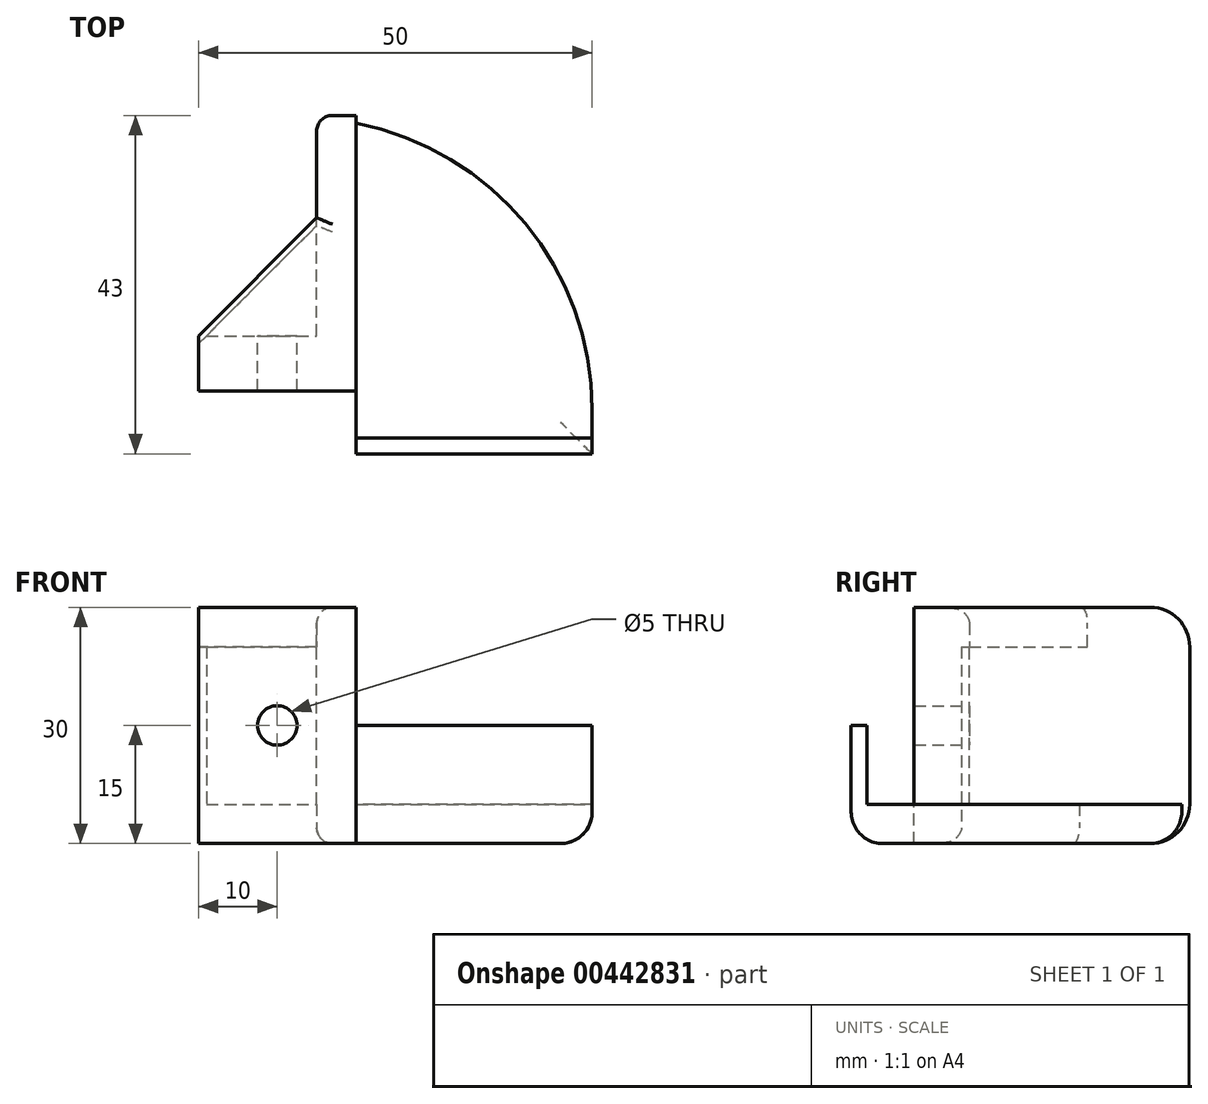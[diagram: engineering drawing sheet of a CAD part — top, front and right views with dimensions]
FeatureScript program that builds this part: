
annotation { "Feature Type Name" : "Feature", "Feature Type Description" : "" }
export const myFeature = defineFeature(function(context is Context, id is Id, definition is map)
    precondition{}
    {
        {
            var Q0;
            Q0=qCreatedBy(makeId("Top.planeOp"),FACE);
            var sketch = newSketch(context, id + "F0", { "sketchPlane" : qUnion([Q0])});
            skLineSegment(sketch, "E0.bottom", {"start": v(0, 0) * mm, "end": v(30, 0) * mm});
            skLineSegment(sketch, "E0.top", {"start": v(0, 42) * mm, "end": v(30, 42) * mm});
            skLineSegment(sketch, "E0.left", {"start": v(0, 0) * mm, "end": v(0, 42) * mm});
            skLineSegment(sketch, "E0.right", {"start": v(30, 0) * mm, "end": v(30, 42) * mm});
            skSolve(sketch);
        }
        {
            var Q0;
            Q0=makeQuery(id+"F0.imprint","IMPRINT",FACE,{"disambiguationData":[TD([[makeQuery(id+"F0.imprint","IMPRINT",EDGE,{"derivedFrom":sQuery(id+"F0.wireOp",EDGE,"E0.bottom")}),1.0]])]});
            extrude(context, id + "F1", {"entities" : qUnion([Q0]), "depth" : 5 * mm});
        }
        {
            var Q0;
            Q0=makeQuery(id+"F1.opExtrude","SWEPT_EDGE",EDGE,{"disambiguationData":[OSD([sQuery(id+"F0.wireOp",EDGE,"E0.top"),sQuery(id+"F0.wireOp",EDGE,"E0.right")])]});
            fillet(context, id + "F2", {"entities" : qUnion([Q0]), "radius" : 37 * mm, "tangentPropagation" : true, "allowEdgeOverflow" : false});
        }
        {
            var Q0;
            Q0=makeQuery(id+"F1.opExtrude","CAP_FACE",FACE,{"disambiguationData":[OSD([sQuery(id+"F0.wireOp",EDGE,"E0.bottom"),sQuery(id+"F0.wireOp",EDGE,"E0.top"),sQuery(id+"F0.wireOp",EDGE,"E0.left"),sQuery(id+"F0.wireOp",EDGE,"E0.right")])],"isStart":false});
            var sketch = newSketch(context, id + "F3", { "sketchPlane" : qUnion([Q0])});
            skLineSegment(sketch, "E1.bottom", {"start": v(0, 0) * mm, "end": v(30, 0) * mm});
            skLineSegment(sketch, "E1.top", {"start": v(0, 2) * mm, "end": v(30, 2) * mm});
            skLineSegment(sketch, "E1.left", {"start": v(0, 0) * mm, "end": v(0, 2) * mm});
            skLineSegment(sketch, "E1.right", {"start": v(30, 0) * mm, "end": v(30, 2) * mm});
            skSolve(sketch);
        }
        {
            var Q0;
            Q0=qSketchRegion(id+"F3",true);
            extrude(context, id + "F4", {"entities" : qUnion([Q0]), "operationType" : NewBodyOperationType.ADD, "depth" : 10 * mm});
        }
        {
            var Q0;
            Q0=makeQuery(id+"F4.boolean.opBoolean","MERGE",FACE,{"derivedFrom":[makeQuery(id+"F1.opExtrude","SWEPT_FACE",FACE,{"disambiguationData":[OSD([sQuery(id+"F0.wireOp",EDGE,"E0.left")])]}),makeQuery(id+"F4.opExtrude","SWEPT_FACE",FACE,{"disambiguationData":[OSD([sQuery(id+"F3.wireOp",EDGE,"E1.left")])]})]});
            var sketch = newSketch(context, id + "F5", { "sketchPlane" : qUnion([Q0])});
            skLineSegment(sketch, "E2.bottom", {"start": v(-8, 0) * mm, "end": v(-43, 0) * mm});
            skLineSegment(sketch, "E2.top", {"start": v(-8, 30) * mm, "end": v(-43, 30) * mm});
            skLineSegment(sketch, "E2.left", {"start": v(-8, 0) * mm, "end": v(-8, 30) * mm});
            skLineSegment(sketch, "E2.right", {"start": v(-43, 0) * mm, "end": v(-43, 30) * mm});
            skSolve(sketch);
        }
        {
            var Q0;
            Q0=qSketchRegion(id+"F5",true);
            extrude(context, id + "F6", {"entities" : qUnion([Q0]), "operationType" : NewBodyOperationType.ADD, "depth" : 5 * mm});
        }
        {
            var Q0;
            Q0=makeQuery(id+"F6.opExtrude","CAP_FACE",FACE,{"disambiguationData":[OSD([sQuery(id+"F5.wireOp",EDGE,"E2.bottom"),sQuery(id+"F5.wireOp",EDGE,"E2.top"),sQuery(id+"F5.wireOp",EDGE,"E2.left"),sQuery(id+"F5.wireOp",EDGE,"E2.right")])],"isStart":false});
            var sketch = newSketch(context, id + "F7", { "sketchPlane" : qUnion([Q0])});
            skLineSegment(sketch, "E3.bottom", {"start": v(-8, 0) * mm, "end": v(-8, 0) * mm});
            skLineSegment(sketch, "E3.top", {"start": v(-8, 30) * mm, "end": v(-8, 30) * mm});
            skLineSegment(sketch, "E3.left", {"start": v(-8, 0) * mm, "end": v(-8, 30) * mm});
            skLineSegment(sketch, "E3.right", {"start": v(-8, 0) * mm, "end": v(-8, 30) * mm});
            skLineSegment(sketch, "E4.bottom", {"start": v(-8, 0) * mm, "end": v(-15, 0) * mm});
            skLineSegment(sketch, "E4.top", {"start": v(-8, 30) * mm, "end": v(-15, 30) * mm});
            skLineSegment(sketch, "E4.right", {"start": v(-15, 0) * mm, "end": v(-15, 30) * mm});
            skSolve(sketch);
        }
        {
            var Q0;
            Q0=qSketchRegion(id+"F7",true);
            extrude(context, id + "F8", {"entities" : qUnion([Q0]), "operationType" : NewBodyOperationType.ADD, "depth" : 15 * mm});
        }
        {
            var Q0;
            Q0=makeQuery(id+"F8.opExtrude","SWEPT_FACE",FACE,{"disambiguationData":[OSD([sQuery(id+"F7.wireOp",EDGE,"E4.right")])]});
            var sketch = newSketch(context, id + "F9", { "sketchPlane" : qUnion([Q0])});
            skCircle(sketch, "E5", {"center": v(10, 15) * mm, "radius": 2.5 * mm});
            skSolve(sketch);
        }
        {
            var Q0;
            Q0=makeQuery(id+"F9.imprint","IMPRINT",FACE,{"disambiguationData":[TD([[makeQuery(id+"F9.imprint","IMPRINT",EDGE,{"derivedFrom":sQuery(id+"F9.wireOp",EDGE,"E5")}),1.0]])]});
            var Q1;
            Q1=sQuery(id+"F9.wireOp",EDGE,"E5");
            extrude(context, id + "F10", {"entities" : qUnion([Q0]), "operationType" : NewBodyOperationType.REMOVE, "surfaceEntities" : qUnion([Q1]), "oppositeDirection" : true, "depth" : 10 * mm});
        }
        {
            var Q0;
            {var subQ0=sQuery(id+"F0.wireOp",EDGE,"E0.right");var subQ1=sQuery(id+"F0.wireOp",EDGE,"E0.top");Q0=makeQuery(id+"F2.opFillet","BLEND_EDGE",EDGE,{"blendedFrom":[makeQuery(id+"F1.opExtrude","SWEPT_EDGE",EDGE,{"disambiguationData":[OSD([subQ1,subQ0])]}),makeQuery(id+"F1.opExtrude","CAP_FACE",FACE,{"disambiguationData":[OSD([sQuery(id+"F0.wireOp",EDGE,"E0.bottom"),subQ1,sQuery(id+"F0.wireOp",EDGE,"E0.left"),subQ0])],"isStart":true})],"blendedInto":[makeQuery(id+"F1.opExtrude","CAP_FACE",FACE,{"disambiguationData":[OSD([sQuery(id+"F0.wireOp",EDGE,"E0.bottom"),subQ1,sQuery(id+"F0.wireOp",EDGE,"E0.left"),subQ0])],"isStart":true})]});}
            var Q1;
            Q1=makeQuery(id+"F1.opExtrude","CAP_EDGE",EDGE,{"disambiguationData":[OSD([sQuery(id+"F0.wireOp",EDGE,"E0.bottom")])],"isStart":true});
            fillet(context, id + "F11", {"entities" : qUnion([Q0, Q1]), "radius" : 4 * mm, "tangentPropagation" : true, "allowEdgeOverflow" : false});
        }
        {
            var Q0;
            Q0=makeQuery(id+"F8.boolean.opBoolean","MERGE",FACE,{"derivedFrom":[makeQuery(id+"F6.boolean.opBoolean","MERGE",FACE,{"derivedFrom":[makeQuery(id+"F1.opExtrude","CAP_FACE",FACE,{"disambiguationData":[OSD([sQuery(id+"F0.wireOp",EDGE,"E0.bottom"),sQuery(id+"F0.wireOp",EDGE,"E0.top"),sQuery(id+"F0.wireOp",EDGE,"E0.left"),sQuery(id+"F0.wireOp",EDGE,"E0.right")])],"isStart":true}),makeQuery(id+"F6.opExtrude","SWEPT_FACE",FACE,{"disambiguationData":[OSD([sQuery(id+"F5.wireOp",EDGE,"E2.bottom")])]})]}),makeQuery(id+"F8.opExtrude","SWEPT_FACE",FACE,{"disambiguationData":[OSD([sQuery(id+"F7.wireOp",EDGE,"E4.bottom")])]})]});
            var sketch = newSketch(context, id + "F12", { "sketchPlane" : qUnion([Q0])});
            skLineSegment(sketch, "E6.bottom", {"start": v(-20, -15) * mm, "end": v(-5, -15) * mm});
            skLineSegment(sketch, "E6.top", {"start": v(-20, -29) * mm, "end": v(-5, -29) * mm});
            skLineSegment(sketch, "E6.left", {"start": v(-20, -15) * mm, "end": v(-20, -29) * mm});
            skLineSegment(sketch, "E6.right", {"start": v(-5, -15) * mm, "end": v(-5, -29) * mm});
            skSolve(sketch);
        }
        {
            var Q0;
            Q0=makeQuery(id+"F12.imprint","IMPRINT",FACE,{"disambiguationData":[TD([[makeQuery(id+"F12.imprint","IMPRINT",EDGE,{"derivedFrom":sQuery(id+"F12.wireOp",EDGE,"E6.bottom")}),-1.0]])]});
            extrude(context, id + "F13", {"entities" : qUnion([Q0]), "operationType" : NewBodyOperationType.ADD, "oppositeDirection" : true, "depth" : 5 * mm});
        }
        {
            var Q0;
            Q0=makeQuery(id+"F8.boolean.opBoolean","MERGE",FACE,{"derivedFrom":[makeQuery(id+"F6.opExtrude","SWEPT_FACE",FACE,{"disambiguationData":[OSD([sQuery(id+"F5.wireOp",EDGE,"E2.top")])]}),makeQuery(id+"F8.opExtrude","SWEPT_FACE",FACE,{"disambiguationData":[OSD([sQuery(id+"F7.wireOp",EDGE,"E4.top")])]})]});
            var sketch = newSketch(context, id + "F14", { "sketchPlane" : qUnion([Q0])});
            skLineSegment(sketch, "E7.bottom", {"start": v(-5, 15) * mm, "end": v(-20, 15) * mm});
            skLineSegment(sketch, "E7.top", {"start": v(-5, 30) * mm, "end": v(-20, 30) * mm});
            skLineSegment(sketch, "E7.left", {"start": v(-5, 15) * mm, "end": v(-5, 30) * mm});
            skLineSegment(sketch, "E7.right", {"start": v(-20, 15) * mm, "end": v(-20, 30) * mm});
            skSolve(sketch);
        }
        {
            var Q0;
            Q0=makeQuery(id+"F14.imprint","IMPRINT",FACE,{"disambiguationData":[TD([[makeQuery(id+"F14.imprint","IMPRINT",EDGE,{"derivedFrom":sQuery(id+"F14.wireOp",EDGE,"E7.bottom")}),1.0]])]});
            extrude(context, id + "F15", {"entities" : qUnion([Q0]), "operationType" : NewBodyOperationType.ADD, "oppositeDirection" : true, "depth" : 5 * mm});
        }
        {
            var Q0;
            Q0=makeQuery(id+"F15.opExtrude","SWEPT_EDGE",EDGE,{"disambiguationData":[OSD([sQuery(id+"F14.wireOp",EDGE,"E7.top"),sQuery(id+"F14.wireOp",EDGE,"E7.right")])]});
            var Q1;
            Q1=makeQuery(id+"F13.opExtrude","SWEPT_EDGE",EDGE,{"disambiguationData":[OSD([sQuery(id+"F12.wireOp",EDGE,"E6.top"),sQuery(id+"F12.wireOp",EDGE,"E6.left")])]});
            chamfer(context, id + "F16", {"entities" : qUnion([Q0, Q1]), "width" : 15 * mm, "tangentPropagation" : true});
        }
        {
            var Q0;
            Q0=makeQuery(id+"F6.opExtrude","SWEPT_EDGE",EDGE,{"disambiguationData":[OSD([sQuery(id+"F5.wireOp",EDGE,"E2.bottom"),sQuery(id+"F5.wireOp",EDGE,"E2.right")])]});
            var Q1;
            Q1=makeQuery(id+"F6.opExtrude","SWEPT_EDGE",EDGE,{"disambiguationData":[OSD([sQuery(id+"F5.wireOp",EDGE,"E2.top"),sQuery(id+"F5.wireOp",EDGE,"E2.right")])]});
            fillet(context, id + "F17", {"entities" : qUnion([Q0, Q1]), "radius" : 5 * mm, "tangentPropagation" : true, "allowEdgeOverflow" : false});
        }
        {
            var Q0;
            Q0=makeQuery(id+"F6.opExtrude","CAP_EDGE",EDGE,{"disambiguationData":[OSD([sQuery(id+"F5.wireOp",EDGE,"E2.right")])],"isStart":false});
            var Q1;
            Q1=makeQuery(id+"F8.opExtrude","CAP_EDGE",EDGE,{"disambiguationData":[OSD([sQuery(id+"F7.wireOp",EDGE,"E4.right")])],"isStart":false});
            var Q2;
            {var subQ0=sQuery(id+"F12.wireOp",EDGE,"E6.left");var subQ1=sQuery(id+"F12.wireOp",EDGE,"E6.top");Q2=makeQuery(id+"F16.opChamfer","BLEND_EDGE",EDGE,{"blendedFrom":[makeQuery(id+"F13.opExtrude","SWEPT_EDGE",EDGE,{"disambiguationData":[OSD([subQ1,subQ0])]}),makeQuery(id+"F13.boolean.opBoolean","MERGE",FACE,{"derivedFrom":[makeQuery(id+"F8.boolean.opBoolean","MERGE",FACE,{"derivedFrom":[makeQuery(id+"F6.boolean.opBoolean","MERGE",FACE,{"derivedFrom":[makeQuery(id+"F1.opExtrude","CAP_FACE",FACE,{"disambiguationData":[OSD([sQuery(id+"F0.wireOp",EDGE,"E0.bottom"),sQuery(id+"F0.wireOp",EDGE,"E0.top"),sQuery(id+"F0.wireOp",EDGE,"E0.left"),sQuery(id+"F0.wireOp",EDGE,"E0.right")])],"isStart":true}),makeQuery(id+"F6.opExtrude","SWEPT_FACE",FACE,{"disambiguationData":[OSD([sQuery(id+"F5.wireOp",EDGE,"E2.bottom")])]})]}),makeQuery(id+"F8.opExtrude","SWEPT_FACE",FACE,{"disambiguationData":[OSD([sQuery(id+"F7.wireOp",EDGE,"E4.bottom")])]})]}),makeQuery(id+"F13.opExtrude","CAP_FACE",FACE,{"disambiguationData":[OSD([sQuery(id+"F12.wireOp",EDGE,"E6.bottom"),subQ1,subQ0,sQuery(id+"F12.wireOp",EDGE,"E6.right")])],"isStart":true})]})],"blendedInto":[makeQuery(id+"F13.boolean.opBoolean","MERGE",FACE,{"derivedFrom":[makeQuery(id+"F8.boolean.opBoolean","MERGE",FACE,{"derivedFrom":[makeQuery(id+"F6.boolean.opBoolean","MERGE",FACE,{"derivedFrom":[makeQuery(id+"F1.opExtrude","CAP_FACE",FACE,{"disambiguationData":[OSD([sQuery(id+"F0.wireOp",EDGE,"E0.bottom"),sQuery(id+"F0.wireOp",EDGE,"E0.top"),sQuery(id+"F0.wireOp",EDGE,"E0.left"),sQuery(id+"F0.wireOp",EDGE,"E0.right")])],"isStart":true}),makeQuery(id+"F6.opExtrude","SWEPT_FACE",FACE,{"disambiguationData":[OSD([sQuery(id+"F5.wireOp",EDGE,"E2.bottom")])]})]}),makeQuery(id+"F8.opExtrude","SWEPT_FACE",FACE,{"disambiguationData":[OSD([sQuery(id+"F7.wireOp",EDGE,"E4.bottom")])]})]}),makeQuery(id+"F13.opExtrude","CAP_FACE",FACE,{"disambiguationData":[OSD([sQuery(id+"F12.wireOp",EDGE,"E6.bottom"),subQ1,subQ0,sQuery(id+"F12.wireOp",EDGE,"E6.right")])],"isStart":true})]})]});}
            var Q3;
            {var subQ0=sQuery(id+"F14.wireOp",EDGE,"E7.right");var subQ1=sQuery(id+"F14.wireOp",EDGE,"E7.top");Q3=makeQuery(id+"F16.opChamfer","BLEND_EDGE",EDGE,{"blendedFrom":[makeQuery(id+"F15.opExtrude","SWEPT_EDGE",EDGE,{"disambiguationData":[OSD([subQ1,subQ0])]}),makeQuery(id+"F15.boolean.opBoolean","MERGE",FACE,{"derivedFrom":[makeQuery(id+"F8.boolean.opBoolean","MERGE",FACE,{"derivedFrom":[makeQuery(id+"F6.opExtrude","SWEPT_FACE",FACE,{"disambiguationData":[OSD([sQuery(id+"F5.wireOp",EDGE,"E2.top")])]}),makeQuery(id+"F8.opExtrude","SWEPT_FACE",FACE,{"disambiguationData":[OSD([sQuery(id+"F7.wireOp",EDGE,"E4.top")])]})]}),makeQuery(id+"F15.opExtrude","CAP_FACE",FACE,{"disambiguationData":[OSD([sQuery(id+"F14.wireOp",EDGE,"E7.bottom"),subQ1,sQuery(id+"F14.wireOp",EDGE,"E7.left"),subQ0])],"isStart":true})]})],"blendedInto":[makeQuery(id+"F15.boolean.opBoolean","MERGE",FACE,{"derivedFrom":[makeQuery(id+"F8.boolean.opBoolean","MERGE",FACE,{"derivedFrom":[makeQuery(id+"F6.opExtrude","SWEPT_FACE",FACE,{"disambiguationData":[OSD([sQuery(id+"F5.wireOp",EDGE,"E2.top")])]}),makeQuery(id+"F8.opExtrude","SWEPT_FACE",FACE,{"disambiguationData":[OSD([sQuery(id+"F7.wireOp",EDGE,"E4.top")])]})]}),makeQuery(id+"F15.opExtrude","CAP_FACE",FACE,{"disambiguationData":[OSD([sQuery(id+"F14.wireOp",EDGE,"E7.bottom"),subQ1,sQuery(id+"F14.wireOp",EDGE,"E7.left"),subQ0])],"isStart":true})]})]});}
            var Q4;
            Q4=makeQuery(id+"F6.opExtrude","CAP_EDGE",EDGE,{"disambiguationData":[OSD([sQuery(id+"F5.wireOp",EDGE,"E2.bottom")])],"isStart":false});
            var Q5;
            {var subQ0=sQuery(id+"F5.wireOp",EDGE,"E2.right");var subQ1=sQuery(id+"F5.wireOp",EDGE,"E2.bottom");Q5=makeQuery(id+"F17.opFillet","BLEND_EDGE",EDGE,{"blendedFrom":[makeQuery(id+"F6.opExtrude","SWEPT_EDGE",EDGE,{"disambiguationData":[OSD([subQ1,subQ0])]}),makeQuery(id+"F6.opExtrude","CAP_FACE",FACE,{"disambiguationData":[OSD([subQ1,sQuery(id+"F5.wireOp",EDGE,"E2.top"),sQuery(id+"F5.wireOp",EDGE,"E2.left"),subQ0])],"isStart":false})],"blendedInto":[makeQuery(id+"F6.opExtrude","CAP_FACE",FACE,{"disambiguationData":[OSD([subQ1,sQuery(id+"F5.wireOp",EDGE,"E2.top"),sQuery(id+"F5.wireOp",EDGE,"E2.left"),subQ0])],"isStart":false})]});}
            var Q6;
            {var subQ0=sQuery(id+"F5.wireOp",EDGE,"E2.right");var subQ1=sQuery(id+"F5.wireOp",EDGE,"E2.top");Q6=makeQuery(id+"F17.opFillet","BLEND_EDGE",EDGE,{"blendedFrom":[makeQuery(id+"F6.opExtrude","SWEPT_EDGE",EDGE,{"disambiguationData":[OSD([subQ1,subQ0])]}),makeQuery(id+"F6.opExtrude","CAP_FACE",FACE,{"disambiguationData":[OSD([sQuery(id+"F5.wireOp",EDGE,"E2.bottom"),subQ1,sQuery(id+"F5.wireOp",EDGE,"E2.left"),subQ0])],"isStart":false})],"blendedInto":[makeQuery(id+"F6.opExtrude","CAP_FACE",FACE,{"disambiguationData":[OSD([sQuery(id+"F5.wireOp",EDGE,"E2.bottom"),subQ1,sQuery(id+"F5.wireOp",EDGE,"E2.left"),subQ0])],"isStart":false})]});}
            var Q7;
            Q7=makeQuery(id+"F6.opExtrude","CAP_EDGE",EDGE,{"disambiguationData":[OSD([sQuery(id+"F5.wireOp",EDGE,"E2.top")])],"isStart":false});
            fillet(context, id + "F18", {"entities" : qUnion([Q0, Q1, Q2, Q3, Q4, Q5, Q6, Q7]), "radius" : 2 * mm, "tangentPropagation" : true, "allowEdgeOverflow" : false});
        }
    });
